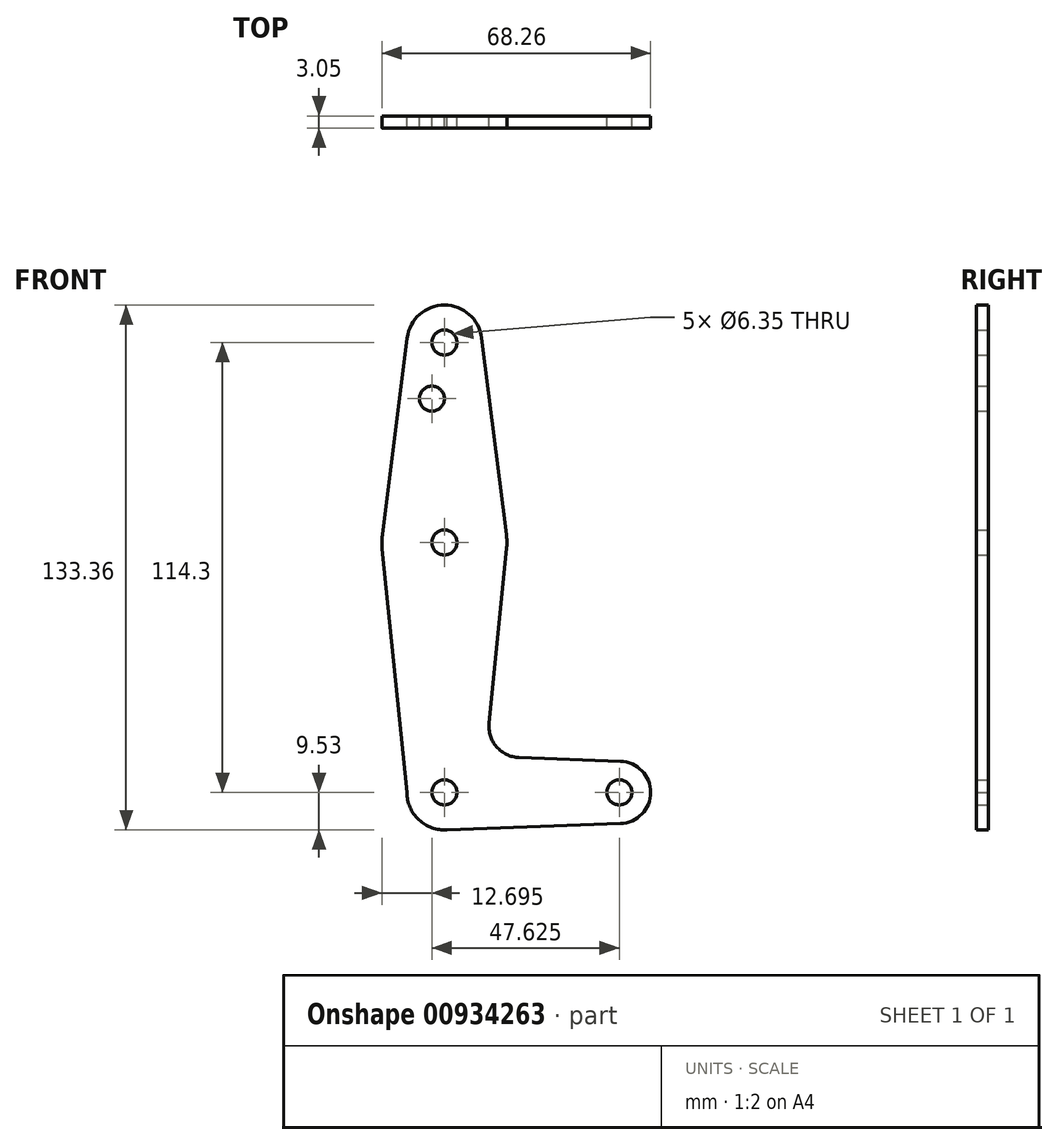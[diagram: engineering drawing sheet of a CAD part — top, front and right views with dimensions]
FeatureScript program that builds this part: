
annotation { "Feature Type Name" : "Feature", "Feature Type Description" : "" }
export const myFeature = defineFeature(function(context is Context, id is Id, definition is map)
    precondition{}
    {
        {
            var Q0;
            Q0=qCreatedBy(makeId("Front.planeOp"),FACE);
            var sketch = newSketch(context, id + "F0", { "sketchPlane" : qUnion([Q0])});
            skCircle(sketch, "E0", {"center": v(0, 0) * mm, "radius": 9.53 * mm});
            skLineSegment(sketch, "E1", {"start": v(0, 114.3) * mm, "end": v(0, 0) * mm, "construction": true});
            skLineSegment(sketch, "E2", {"start": v(0, 0) * mm, "end": v(44.45, 0) * mm, "construction": true});
            skCircle(sketch, "E3", {"center": v(0, 63.5) * mm, "radius": 15.88 * mm});
            skCircle(sketch, "E4", {"center": v(0, 114.3) * mm, "radius": 9.53 * mm});
            skCircle(sketch, "E5", {"center": v(44.45, 0) * mm, "radius": 7.94 * mm});
            skLineSegment(sketch, "E6", {"start": v(0, -9.52) * mm, "end": v(44.73, -7.93) * mm});
            skLineSegment(sketch, "E7", {"start": v(-9.52, 0) * mm, "end": v(-15.8, 61.9) * mm});
            skLineSegment(sketch, "E8", {"start": v(9.45, 115.5) * mm, "end": v(15.75, 65.48) * mm});
            skLineSegment(sketch, "E9", {"start": v(-9.45, 115.5) * mm, "end": v(-15.75, 65.48) * mm});
            skCircle(sketch, "E10", {"center": v(0, 114.3) * mm, "radius": 3.18 * mm});
            skCircle(sketch, "E11", {"center": v(-3.17, 100.03) * mm, "radius": 3.18 * mm});
            skCircle(sketch, "E12", {"center": v(0, 63.5) * mm, "radius": 3.18 * mm});
            skCircle(sketch, "E13", {"center": v(0, 0) * mm, "radius": 3.18 * mm});
            skCircle(sketch, "E14", {"center": v(44.45, 0) * mm, "radius": 3.18 * mm});
            skLineSegment(sketch, "E15", {"start": v(15.8, 61.91) * mm, "end": v(11.34, 17.6) * mm});
            skLineSegment(sketch, "E16", {"start": v(44.73, 7.93) * mm, "end": v(18.97, 8.85) * mm});
            skArc(sketch, "E17.filletArc", {"start": v(11.34, 17.6) * mm, "mid": v(13.26, 11.57) * mm, "end": v(18.97, 8.85) * mm});
            skSolve(sketch);
        }
        {
            var Q0;
            Q0 = qSketchRegion(id + "F0", true);
            extrude(context, id + "F1", {"entities" : qUnion([Q0]), "depth" : 3.05 * mm, "offsetDistance" : 25.4 * mm});
        }
    });
